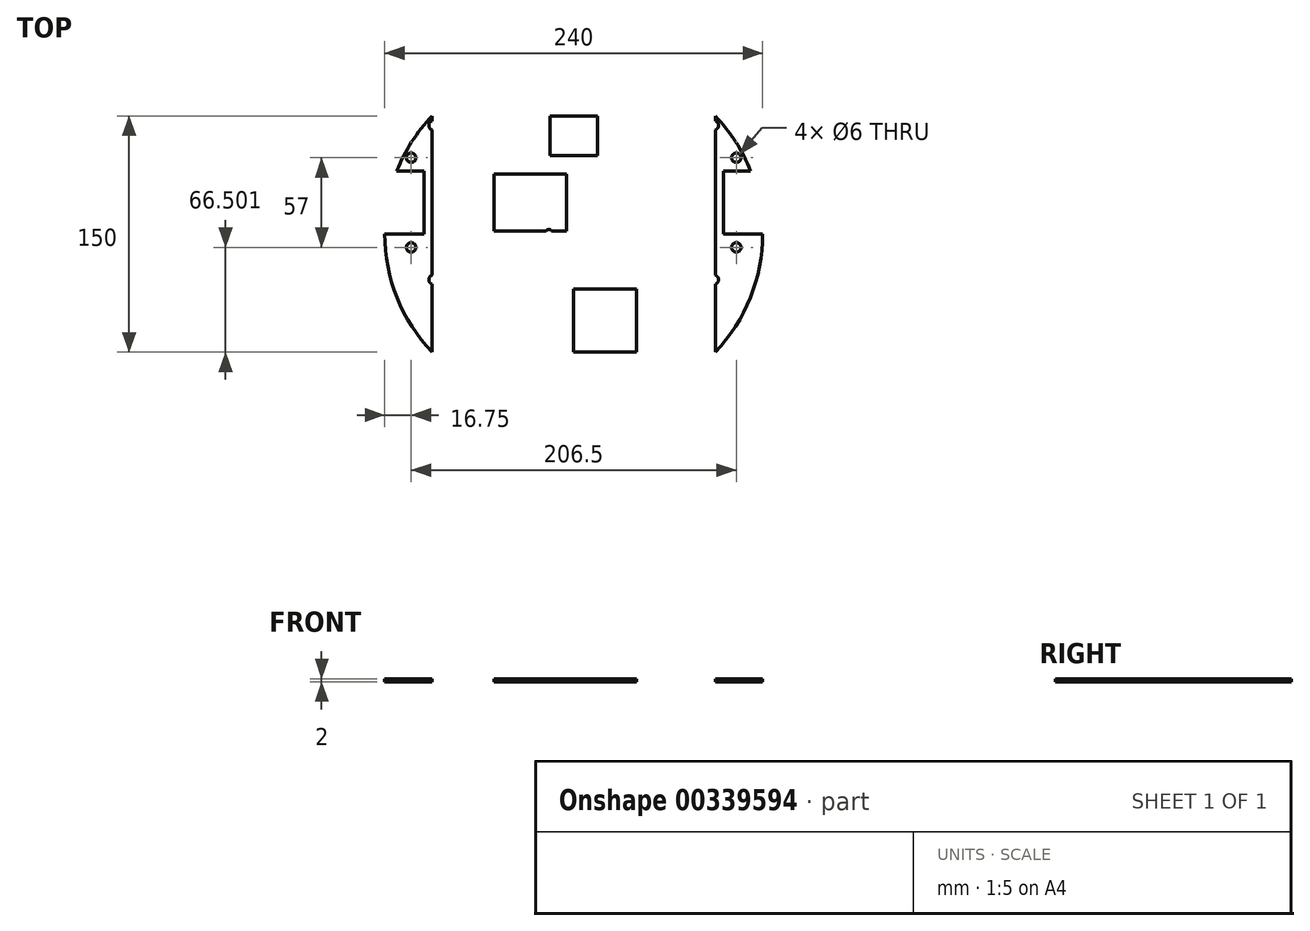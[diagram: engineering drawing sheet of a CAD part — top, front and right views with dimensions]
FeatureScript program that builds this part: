
annotation { "Feature Type Name" : "Feature", "Feature Type Description" : "" }
export const myFeature = defineFeature(function(context is Context, id is Id, definition is map)
    precondition{}
    {
        {
            var Q0;
            Q0=qCreatedBy(makeId("Top.planeOp"),FACE);
            var sketch = newSketch(context, id + "F0", { "sketchPlane" : qUnion([Q0])});
            skLineSegment(sketch, "E0.bottom", {"start": v(0, 103.91) * mm, "end": v(-90, 103.91) * mm});
            skLineSegment(sketch, "E0.top", {"start": v(0, -46.09) * mm, "end": v(-90, -46.09) * mm});
            skLineSegment(sketch, "E0.left", {"start": v(0, 103.91) * mm, "end": v(0, -46.09) * mm});
            skLineSegment(sketch, "E0.right", {"start": v(-90, 103.91) * mm, "end": v(-90, -46.09) * mm});
            skArc(sketch, "E1", {"start": v(-90, 103.91) * mm, "mid": v(-120, 28.91) * mm, "end": v(-90, -46.09) * mm});
            skLineSegment(sketch, "E2.bottom", {"start": v(-15, 103.91) * mm, "end": v(0, 103.91) * mm});
            skLineSegment(sketch, "E2.top", {"start": v(-15, 78.91) * mm, "end": v(0, 78.91) * mm});
            skLineSegment(sketch, "E2.left", {"start": v(-15, 103.91) * mm, "end": v(-15, 78.91) * mm});
            skLineSegment(sketch, "E2.right", {"start": v(0, 103.91) * mm, "end": v(0, 78.91) * mm});
            skPoint(sketch, "E3.firstSnap0", {"position": v(-120, 28.91) * mm});
            skLineSegment(sketch, "E3.bottom", {"start": v(-120, 28.91) * mm, "end": v(-95, 28.91) * mm});
            skLineSegment(sketch, "E3.top", {"start": v(-120, 68.91) * mm, "end": v(-95, 68.91) * mm});
            skLineSegment(sketch, "E3.left", {"start": v(-120, 28.91) * mm, "end": v(-120, 68.91) * mm});
            skLineSegment(sketch, "E3.right", {"start": v(-95, 28.91) * mm, "end": v(-95, 68.91) * mm});
            skLineSegment(sketch, "E4.MirrorCS", {"start": v(0, 103.91) * mm, "end": v(90, 103.91) * mm});
            skLineSegment(sketch, "E5.MirrorCS", {"start": v(0, -46.09) * mm, "end": v(90, -46.09) * mm});
            skLineSegment(sketch, "E6.MirrorCS", {"start": v(90, 103.91) * mm, "end": v(90, -46.09) * mm});
            skArc(sketch, "E7.MirrorCS", {"start": v(90, 103.91) * mm, "mid": v(120, 28.91) * mm, "end": v(90, -46.09) * mm});
            skPoint(sketch, "E8.MirrorP", {"position": v(120, 28.91) * mm});
            skLineSegment(sketch, "E9.MirrorCS", {"start": v(95, 28.91) * mm, "end": v(95, 68.91) * mm});
            skLineSegment(sketch, "E10.MirrorCS", {"start": v(120, 28.91) * mm, "end": v(120, 68.91) * mm});
            skLineSegment(sketch, "E11.MirrorCS", {"start": v(15, 103.91) * mm, "end": v(0, 103.91) * mm});
            skLineSegment(sketch, "E12.MirrorCS", {"start": v(15, 78.91) * mm, "end": v(0, 78.91) * mm});
            skLineSegment(sketch, "E13.MirrorCS", {"start": v(120, 68.91) * mm, "end": v(95, 68.91) * mm});
            skLineSegment(sketch, "E14.MirrorCS", {"start": v(120, 28.91) * mm, "end": v(95, 28.91) * mm});
            skLineSegment(sketch, "E15.MirrorCS", {"start": v(15, 103.91) * mm, "end": v(15, 78.91) * mm});
            skLineSegment(sketch, "E16.bottom", {"start": v(0, -46.09) * mm, "end": v(-40, -46.09) * mm});
            skLineSegment(sketch, "E16.top", {"start": v(0, -6.09) * mm, "end": v(-40, -6.09) * mm});
            skLineSegment(sketch, "E16.left", {"start": v(0, -46.09) * mm, "end": v(0, -6.09) * mm});
            skLineSegment(sketch, "E16.right", {"start": v(-40, -46.09) * mm, "end": v(-40, -6.09) * mm});
            skLineSegment(sketch, "E17.MirrorCS", {"start": v(0, -46.09) * mm, "end": v(40, -46.09) * mm});
            skLineSegment(sketch, "E18.MirrorCS", {"start": v(40, -46.09) * mm, "end": v(40, -6.09) * mm});
            skLineSegment(sketch, "E19.MirrorCS", {"start": v(0, -6.09) * mm, "end": v(40, -6.09) * mm});
            skCircle(sketch, "E20", {"center": v(-55.75, 68.91) * mm, "radius": 2 * mm});
            skCircle(sketch, "E21", {"center": v(-15.75, 68.91) * mm, "radius": 2 * mm});
            skCircle(sketch, "E22", {"center": v(-55.75, 29.91) * mm, "radius": 2 * mm});
            skCircle(sketch, "E23", {"center": v(-15.75, 29.91) * mm, "radius": 2 * mm});
            skCircle(sketch, "E24.MirrorC", {"center": v(55.75, 29.91) * mm, "radius": 2 * mm});
            skCircle(sketch, "E25.MirrorC", {"center": v(55.75, 68.91) * mm, "radius": 2 * mm});
            skCircle(sketch, "E26.MirrorC", {"center": v(15.75, 68.91) * mm, "radius": 2 * mm});
            skCircle(sketch, "E27.MirrorC", {"center": v(15.75, 29.91) * mm, "radius": 2 * mm});
            skLineSegment(sketch, "E28.bottom", {"start": v(-96.5, 83.91) * mm, "end": v(-56.5, 83.91) * mm, "construction": true});
            skLineSegment(sketch, "E28.top", {"start": v(-96.5, 13.91) * mm, "end": v(-56.5, 13.91) * mm, "construction": true});
            skLineSegment(sketch, "E28.left", {"start": v(-96.5, 83.91) * mm, "end": v(-96.5, 13.91) * mm, "construction": true});
            skLineSegment(sketch, "E28.right", {"start": v(-56.5, 83.91) * mm, "end": v(-56.5, 13.91) * mm, "construction": true});
            skLineSegment(sketch, "E29.bottom", {"start": v(-50.5, 66.91) * mm, "end": v(-4.7, 66.91) * mm});
            skLineSegment(sketch, "E29.top", {"start": v(-50.5, 30.91) * mm, "end": v(-4.7, 30.91) * mm});
            skLineSegment(sketch, "E29.left", {"start": v(-50.5, 66.91) * mm, "end": v(-50.5, 30.91) * mm});
            skLineSegment(sketch, "E29.right", {"start": v(-4.7, 66.91) * mm, "end": v(-4.7, 30.91) * mm});
            skPoint(sketch, "E30", {"position": v(-56.5, 48.91) * mm});
            skPoint(sketch, "E31", {"position": v(-50.5, 48.91) * mm});
            skCircle(sketch, "E32", {"center": v(-89, -0.09) * mm, "radius": 3 * mm});
            skCircle(sketch, "E33", {"center": v(-103.25, 20.41) * mm, "radius": 3 * mm});
            skPoint(sketch, "E34", {"position": v(-96.5, 48.91) * mm});
            skLineSegment(sketch, "E35", {"start": v(-96.5, 48.91) * mm, "end": v(-56.5, 48.91) * mm, "construction": true});
            skCircle(sketch, "E36", {"center": v(-103.25, 77.41) * mm, "radius": 3 * mm});
            skCircle(sketch, "E37", {"center": v(-89, 97.91) * mm, "radius": 3 * mm});
            skCircle(sketch, "E38", {"center": v(-50, 81.41) * mm, "radius": 3 * mm});
            skCircle(sketch, "E39", {"center": v(-50, 16.41) * mm, "radius": 3 * mm});
            skCircle(sketch, "E40.MirrorC", {"center": v(50, 16.41) * mm, "radius": 3 * mm});
            skCircle(sketch, "E41.MirrorC", {"center": v(89, -0.09) * mm, "radius": 3 * mm});
            skCircle(sketch, "E42.MirrorC", {"center": v(103.25, 77.41) * mm, "radius": 3 * mm});
            skCircle(sketch, "E43.MirrorC", {"center": v(89, 97.91) * mm, "radius": 3 * mm});
            skCircle(sketch, "E44.MirrorC", {"center": v(50, 81.41) * mm, "radius": 3 * mm});
            skCircle(sketch, "E45.MirrorC", {"center": v(103.25, 20.41) * mm, "radius": 3 * mm});
            skSolve(sketch);
        }
        {
            var Q0;
            {var subQ17=sQuery(id+"F0.wireOp",EDGE,"E0.bottom");Q0=makeQuery(id+"F0.imprint","IMPRINT",FACE,{"disambiguationData":[TD([[makeQuery(id+"F0.imprint","IMPRINT",EDGE,{"derivedFrom":subQ17}),1.0]])]});}
            var Q1;
            Q1=makeQuery(id+"F0.imprint","IMPRINT",FACE,{"disambiguationData":[TD([[makeQuery(id+"F0.imprint","IMPRINT",EDGE,{"derivedFrom":sQuery(id+"F0.wireOp",EDGE,"E0.left")}),1.0]])]});
            var Q2;
            {var subQ6=sQuery(id+"F0.wireOp",EDGE,"E9.MirrorCS");Q2=makeQuery(id+"F0.imprint","IMPRINT",FACE,{"disambiguationData":[TD([[makeQuery(id+"F0.imprint","IMPRINT",EDGE,{"derivedFrom":subQ6}),1.0]])]});}
            var Q3;
            {var subQ17=sQuery(id+"F0.wireOp",EDGE,"E0.bottom");Q3=makeQuery(id+"F0.imprint","IMPRINT",FACE,{"disambiguationData":[TD([[makeQuery(id+"F0.imprint","IMPRINT",EDGE,{"derivedFrom":subQ17}),1.0]])]});}
            var Q4;
            {var subQ17=sQuery(id+"F0.wireOp",EDGE,"E0.bottom");Q4=makeQuery(id+"F0.imprint","IMPRINT",FACE,{"disambiguationData":[TD([[makeQuery(id+"F0.imprint","IMPRINT",EDGE,{"derivedFrom":subQ17}),1.0]])]});}
            var Q5;
            {var subQ0=sQuery(id+"F0.wireOp",EDGE,"E29.left");Q5=makeQuery(id+"F0.imprint","IMPRINT",FACE,{"disambiguationData":[TD([[makeQuery(id+"F0.imprint","IMPRINT",EDGE,{"derivedFrom":subQ0}),1.0]])]});}
            var Q6;
            {var subQ6=sQuery(id+"F0.wireOp",EDGE,"E3.bottom");Q6=makeQuery(id+"F0.imprint","IMPRINT",FACE,{"disambiguationData":[TD([[makeQuery(id+"F0.imprint","IMPRINT",EDGE,{"derivedFrom":subQ6}),-1.0]])]});}
            var Q7;
            {var subQ6=sQuery(id+"F0.wireOp",EDGE,"E3.bottom");Q7=makeQuery(id+"F0.imprint","IMPRINT",FACE,{"disambiguationData":[TD([[makeQuery(id+"F0.imprint","IMPRINT",EDGE,{"derivedFrom":subQ6}),-1.0]])]});}
            var Q8;
            {var subQ17=sQuery(id+"F0.wireOp",EDGE,"E0.bottom");Q8=makeQuery(id+"F0.imprint","IMPRINT",FACE,{"disambiguationData":[TD([[makeQuery(id+"F0.imprint","IMPRINT",EDGE,{"derivedFrom":subQ17}),1.0]])]});}
            extrude(context, id + "F1", {"entities" : qUnion([Q0, Q1, Q2, Q3, Q4, Q5, Q6, Q7, Q8]), "depth" : 2 * mm});
        }
    });
